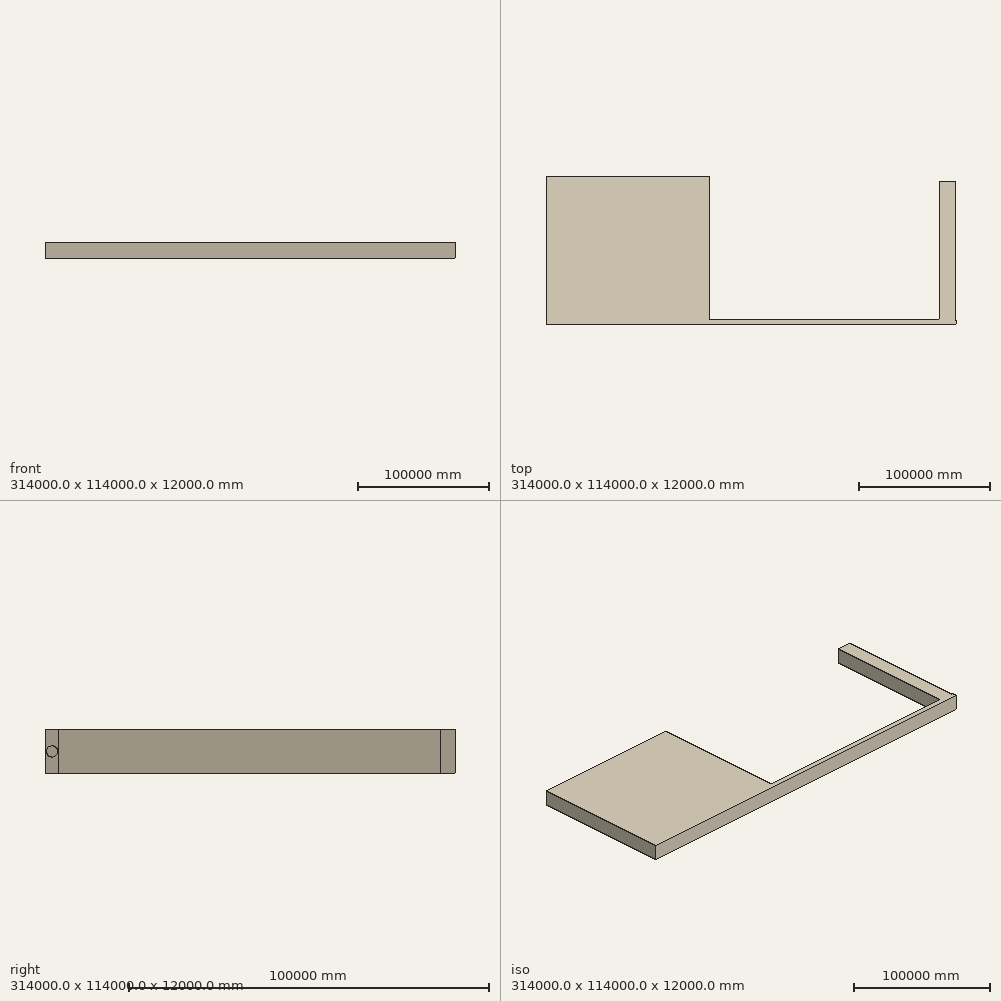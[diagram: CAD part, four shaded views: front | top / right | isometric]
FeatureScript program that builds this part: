
annotation { "Feature Type Name" : "Feature", "Feature Type Description" : "" }
export const myFeature = defineFeature(function(context is Context, id is Id, definition is map)
    precondition{}
    {
        {
            var Q0;
            Q0=qCreatedBy(makeId("Right.planeOp"),FACE);
            var sketch = newSketch(context, id + "F0", { "sketchPlane" : qUnion([Q0])});
            skLineSegment(sketch, "E0.bottom", {"start": v(1700, 5700) * mm, "end": v(-1700, 5700) * mm});
            skLineSegment(sketch, "E0.top", {"start": v(1700, -5700) * mm, "end": v(-1700, -5700) * mm});
            skLineSegment(sketch, "E0.left", {"start": v(1700, 5700) * mm, "end": v(1700, -5700) * mm});
            skLineSegment(sketch, "E0.right", {"start": v(-1700, 5700) * mm, "end": v(-1700, -5700) * mm});
            skPoint(sketch, "E0.middle", {"position": v(0, 0) * mm});
            skSolve(sketch);
        }
        {
            var Q0;
            Q0=makeQuery(id+"F0.imprint","IMPRINT",FACE,{"disambiguationData":[TD([[makeQuery(id+"F0.imprint","IMPRINT",EDGE,{"derivedFrom":sQuery(id+"F0.wireOp",EDGE,"E0.bottom")}),1.0]])]});
            var sketch = newSketch(context, id + "F1", { "sketchPlane" : qUnion([Q0])});
            skLineSegment(sketch, "E1.bottom", {"start": v(2000, 6000) * mm, "end": v(-2000, 6000) * mm});
            skLineSegment(sketch, "E1.top", {"start": v(2000, -6000) * mm, "end": v(-2000, -6000) * mm});
            skLineSegment(sketch, "E1.left", {"start": v(2000, 6000) * mm, "end": v(2000, -6000) * mm});
            skLineSegment(sketch, "E1.right", {"start": v(-2000, 6000) * mm, "end": v(-2000, -6000) * mm});
            skPoint(sketch, "E1.middle", {"position": v(0, 0) * mm});
            skSolve(sketch);
        }
        {
            var Q0;
            Q0=makeQuery(id+"F1.imprint","IMPRINT",FACE,{"disambiguationData":[TD([[makeQuery(id+"F1.imprint","IMPRINT",EDGE,{"derivedFrom":sQuery(id+"F1.wireOp",EDGE,"E1.bottom")}),1.0]])]});
            extrude(context, id + "F2", {"entities" : qUnion([Q0]), "oppositeDirection" : true, "depth" : 200000 * mm, "offsetDistance" : 25 * mm});
        }
        {
            var Q0;
            Q0=makeQuery(id+"F2.opExtrude","SWEPT_FACE",FACE,{"disambiguationData":[OSD([sQuery(id+"F1.wireOp",EDGE,"E1.left")])]});
            var sketch = newSketch(context, id + "F3", { "sketchPlane" : qUnion([Q0])});
            skCircle(sketch, "E2", {"center": v(-6000, 0) * mm, "radius": 6000 * mm});
            skCircle(sketch, "E3", {"center": v(-6000, 0) * mm, "radius": 5475 * mm});
            skLineSegment(sketch, "E4", {"start": v(0, 6000) * mm, "end": v(-6000, 6000) * mm});
            skLineSegment(sketch, "E5", {"start": v(0, -6000) * mm, "end": v(-6000, -6000) * mm});
            skLineSegment(sketch, "E6", {"start": v(-6000, 6000) * mm, "end": v(-12000, 6000) * mm});
            skLineSegment(sketch, "E7", {"start": v(-12000, 6000) * mm, "end": v(-12000, 0) * mm});
            skLineSegment(sketch, "E8", {"start": v(-12000, 0) * mm, "end": v(-12000, -6000) * mm});
            skLineSegment(sketch, "E9", {"start": v(-12000, -6000) * mm, "end": v(-6000, -6000) * mm});
            skSolve(sketch);
        }
        {
            var Q0;
            {var subQ0=sQuery(id+"F3.wireOp",EDGE,"E4");Q0=makeQuery(id+"F3.imprint","IMPRINT",FACE,{"disambiguationData":[TD([[makeQuery(id+"F3.imprint","IMPRINT",EDGE,{"derivedFrom":subQ0}),1.0]])]});}
            var Q1;
            {var subQ0=sQuery(id+"F3.wireOp",EDGE,"E6");Q1=makeQuery(id+"F3.imprint","IMPRINT",FACE,{"disambiguationData":[TD([[makeQuery(id+"F3.imprint","IMPRINT",EDGE,{"derivedFrom":subQ0}),1.0]])]});}
            var Q2;
            {var subQ2=sQuery(id+"F3.wireOp",EDGE,"E8");Q2=makeQuery(id+"F3.imprint","IMPRINT",FACE,{"disambiguationData":[TD([[makeQuery(id+"F3.imprint","IMPRINT",EDGE,{"derivedFrom":subQ2}),1.0]])]});}
            var Q3;
            {var subQ0=sQuery(id+"F3.wireOp",EDGE,"E5");Q3=makeQuery(id+"F3.imprint","IMPRINT",FACE,{"disambiguationData":[TD([[makeQuery(id+"F3.imprint","IMPRINT",EDGE,{"derivedFrom":subQ0}),-1.0]])]});}
            var Q4;
            Q4=makeQuery(id+"F3.imprint","IMPRINT",FACE,{"disambiguationData":[TD([[makeQuery(id+"F3.imprint","IMPRINT",EDGE,{"derivedFrom":sQuery(id+"F3.wireOp",EDGE,"E3")}),-1.0]])]});
            extrude(context, id + "F4", {"entities" : qUnion([Q0, Q1, Q2, Q3, Q4]), "operationType" : NewBodyOperationType.ADD, "oppositeDirection" : true, "depth" : 600 * mm, "offsetDistance" : 25 * mm});
        }
        {
            var Q0;
            Q0=makeQuery(id+"F4.opExtrude","CAP_FACE",FACE,{"disambiguationData":[OSD([sQuery(id+"F1.wireOp",EDGE,"E1.left"),sQuery(id+"F3.wireOp",EDGE,"E3"),sQuery(id+"F3.wireOp",EDGE,"E4"),sQuery(id+"F3.wireOp",EDGE,"E5"),sQuery(id+"F3.wireOp",EDGE,"E6"),sQuery(id+"F3.wireOp",EDGE,"E7"),sQuery(id+"F3.wireOp",EDGE,"E8"),sQuery(id+"F3.wireOp",EDGE,"E9")])],"isStart":false});
            extrude(context, id + "F5", {"entities" : qUnion([Q0]), "operationType" : NewBodyOperationType.ADD, "oppositeDirection" : true, "depth" : 105500 * mm, "offsetDistance" : 25 * mm});
        }
        {
            var Q0;
            Q0=makeQuery(id+"F2.opExtrude","CAP_FACE",FACE,{"disambiguationData":[OSD([sQuery(id+"F0.wireOp",EDGE,"E0.bottom"),sQuery(id+"F0.wireOp",EDGE,"E0.top"),sQuery(id+"F0.wireOp",EDGE,"E0.left"),sQuery(id+"F0.wireOp",EDGE,"E0.right"),sQuery(id+"F1.wireOp",EDGE,"E1.bottom"),sQuery(id+"F1.wireOp",EDGE,"E1.top"),sQuery(id+"F1.wireOp",EDGE,"E1.left"),sQuery(id+"F1.wireOp",EDGE,"E1.right")])],"isStart":true});
            extrude(context, id + "F6", {"entities" : qUnion([Q0]), "operationType" : NewBodyOperationType.ADD, "depth" : 12000 * mm, "offsetDistance" : 25 * mm});
        }
        {
            var Q0;
            {var subQ0=sQuery(id+"F3.wireOp",EDGE,"E8");var subQ1=sQuery(id+"F3.wireOp",EDGE,"E7");Q0=makeQuery(id+"F6.boolean.opBoolean","MERGE",FACE,{"derivedFrom":[makeQuery(id+"F5.boolean.opBoolean","MERGE",FACE,{"derivedFrom":[makeQuery(id+"F4.opExtrude","SWEPT_FACE",FACE,{"disambiguationData":[OSD([subQ1,subQ0])]}),makeQuery(id+"F5.opExtrude","SWEPT_FACE",FACE,{"disambiguationData":[OSD([subQ1,subQ0])]})]}),makeQuery(id+"F6.opExtrude","CAP_FACE",FACE,{"disambiguationData":[OSD([sQuery(id+"F0.wireOp",EDGE,"E0.bottom"),sQuery(id+"F0.wireOp",EDGE,"E0.top"),sQuery(id+"F0.wireOp",EDGE,"E0.left"),sQuery(id+"F0.wireOp",EDGE,"E0.right"),sQuery(id+"F1.wireOp",EDGE,"E1.bottom"),sQuery(id+"F1.wireOp",EDGE,"E1.top"),sQuery(id+"F1.wireOp",EDGE,"E1.left"),sQuery(id+"F1.wireOp",EDGE,"E1.right")])],"isStart":false})]});}
            var sketch = newSketch(context, id + "F7", { "sketchPlane" : qUnion([Q0])});
            skCircle(sketch, "E10", {"center": v(-150, 0) * mm, "radius": 1850 * mm});
            skCircle(sketch, "E11", {"center": v(-150, 0) * mm, "radius": 1550 * mm});
            skLineSegment(sketch, "E12", {"start": v(1700, 0) * mm, "end": v(1700, 6000) * mm});
            skLineSegment(sketch, "E13", {"start": v(1700, 6000) * mm, "end": v(-2000, 6000) * mm});
            skLineSegment(sketch, "E14", {"start": v(-2000, 6000) * mm, "end": v(-2000, 0) * mm});
            skLineSegment(sketch, "E15", {"start": v(-2000, 0) * mm, "end": v(-2000, -6000) * mm});
            skLineSegment(sketch, "E16", {"start": v(-2000, -6000) * mm, "end": v(1700, -6000) * mm});
            skLineSegment(sketch, "E17", {"start": v(1700, -6000) * mm, "end": v(1700, 0) * mm});
            skSolve(sketch);
        }
        {
            var Q0;
            {var subQ0=sQuery(id+"F7.wireOp",EDGE,"E12");Q0=makeQuery(id+"F7.imprint","IMPRINT",FACE,{"disambiguationData":[TD([[makeQuery(id+"F7.imprint","IMPRINT",EDGE,{"derivedFrom":subQ0}),1.0]])]});}
            var Q1;
            {var subQ5=makeQuery(id+"F6.opExtrude","CAP_EDGE",EDGE,{"disambiguationData":[OSD([sQuery(id+"F0.wireOp",EDGE,"E0.bottom")])],"isStart":false});Q1=makeQuery(id+"F7.imprint","IMPRINT",FACE,{"disambiguationData":[TD([[makeQuery(id+"F7.imprint","IMPRINT",EDGE,{"derivedFrom":subQ5}),1.0]])]});}
            var Q2;
            {var subQ5=makeQuery(id+"F6.opExtrude","CAP_EDGE",EDGE,{"disambiguationData":[OSD([sQuery(id+"F0.wireOp",EDGE,"E0.top")])],"isStart":false});Q2=makeQuery(id+"F7.imprint","IMPRINT",FACE,{"disambiguationData":[TD([[makeQuery(id+"F7.imprint","IMPRINT",EDGE,{"derivedFrom":subQ5}),-1.0]])]});}
            var Q3;
            {var subQ0=sQuery(id+"F7.wireOp",EDGE,"E15");Q3=makeQuery(id+"F7.imprint","IMPRINT",FACE,{"disambiguationData":[TD([[makeQuery(id+"F7.imprint","IMPRINT",EDGE,{"derivedFrom":subQ0}),1.0]])]});}
            var Q4;
            {var subQ0=sQuery(id+"F7.wireOp",EDGE,"E10");var subQ1=makeQuery(id+"F7.imprint","INTERSECT",VERTEX,{"derivedFrom":[subQ0,sQuery(id+"F7.wireOp",EDGE,"E12"),sQuery(id+"F7.wireOp",EDGE,"E17")]});Q4=makeQuery(id+"F7.imprint","IMPRINT",FACE,{"disambiguationData":[TD([[makeQuery(id+"F7.imprint","IMPRINT",EDGE,{"disambiguationData":[TD([[subQ1,-1.0]])],"derivedFrom":subQ0}),1.0]])]});}
            var Q5;
            {var subQ0=sQuery(id+"F7.wireOp",EDGE,"E10");var subQ2=makeQuery(id+"F6.opExtrude","CAP_EDGE",EDGE,{"disambiguationData":[OSD([sQuery(id+"F0.wireOp",EDGE,"E0.right")])],"isStart":false});var subQ3=makeQuery(id+"F7.imprint","INTERSECT",VERTEX,{"disambiguationData":[OD(0.0)],"derivedFrom":[subQ2,subQ0]});Q5=makeQuery(id+"F7.imprint","IMPRINT",FACE,{"disambiguationData":[TD([[makeQuery(id+"F7.imprint","IMPRINT",EDGE,{"disambiguationData":[TD([[subQ3,-1.0]])],"derivedFrom":subQ2}),-1.0]])]});}
            var Q6;
            {var subQ0=sQuery(id+"F7.wireOp",EDGE,"E10");var subQ3=makeQuery(id+"F6.opExtrude","CAP_EDGE",EDGE,{"disambiguationData":[OSD([sQuery(id+"F0.wireOp",EDGE,"E0.right")])],"isStart":false});var subQ4=makeQuery(id+"F7.imprint","INTERSECT",VERTEX,{"disambiguationData":[OD(0.0)],"derivedFrom":[subQ3,subQ0]});Q6=makeQuery(id+"F7.imprint","IMPRINT",FACE,{"disambiguationData":[TD([[makeQuery(id+"F7.imprint","IMPRINT",EDGE,{"disambiguationData":[TD([[subQ4,-1.0]])],"derivedFrom":subQ3}),1.0]])]});}
            var Q7;
            {var subQ0=sQuery(id+"F7.wireOp",EDGE,"E10");var subQ1=makeQuery(id+"F6.opExtrude","CAP_EDGE",EDGE,{"disambiguationData":[OSD([sQuery(id+"F0.wireOp",EDGE,"E0.right")])],"isStart":false});var subQ2=makeQuery(id+"F7.imprint","INTERSECT",VERTEX,{"disambiguationData":[OD(1.0)],"derivedFrom":[subQ1,subQ0]});Q7=makeQuery(id+"F7.imprint","IMPRINT",FACE,{"disambiguationData":[TD([[makeQuery(id+"F7.imprint","IMPRINT",EDGE,{"disambiguationData":[TD([[subQ2,1.0]])],"derivedFrom":subQ1}),1.0]])]});}
            extrude(context, id + "F8", {"entities" : qUnion([Q0, Q1, Q2, Q3, Q4, Q5, Q6, Q7]), "operationType" : NewBodyOperationType.ADD, "depth" : 1000 * mm, "offsetDistance" : 25 * mm});
        }
        {
            var Q0;
            Q0=makeQuery(id+"F8.opExtrude","CAP_FACE",FACE,{"disambiguationData":[OSD([sQuery(id+"F7.wireOp",EDGE,"E11"),sQuery(id+"F7.wireOp",EDGE,"E12"),sQuery(id+"F7.wireOp",EDGE,"E13"),sQuery(id+"F7.wireOp",EDGE,"E14"),sQuery(id+"F7.wireOp",EDGE,"E15"),sQuery(id+"F7.wireOp",EDGE,"E16"),sQuery(id+"F7.wireOp",EDGE,"E17")])],"isStart":false});
            cPlane(context, id + "F9", {"entities" : qUnion([Q0]), "cplaneType" : CPlaneType.OFFSET, "offset" : 150000 * mm, "width" : 150 * mm, "height" : 150 * mm});
        }
        {
            var Q0;
            Q0=qCreatedBy(id+"F9.planeOp",FACE);
            var sketch = newSketch(context, id + "F10", { "sketchPlane" : qUnion([Q0])});
            skPoint(sketch, "E18", {"position": v(-150, 0) * mm});
            skPoint(sketch, "E19", {"position": v(-150150, 0) * mm});
            skCircle(sketch, "E20", {"center": v(-150150, 0) * mm, "radius": 1850 * mm});
            skCircle(sketch, "E21", {"center": v(-150150, 0) * mm, "radius": 1550 * mm});
            skSolve(sketch);
        }
        {
            var Q0;
            Q0=makeQuery(id+"F8.opExtrude","CAP_EDGE",EDGE,{"disambiguationData":[OSD([sQuery(id+"F7.wireOp",EDGE,"E11")])],"isStart":false});
            var Q1;
            Q1=sQuery(id+"F10.wireOp",EDGE,"E21");
            loft(context, id + "F11", {"bodyType" : ToolBodyType.SURFACE, "wireProfilesArray" : [{ "wireProfileEntities" : qUnion([Q0]) }, { "wireProfileEntities" : qUnion([Q1]) }]});
        }
        {
            var Q0;
            Q0=makeQuery(id+"F5.opExtrude","CAP_FACE",FACE,{"disambiguationData":[OSD([sQuery(id+"F1.wireOp",EDGE,"E1.left"),sQuery(id+"F3.wireOp",EDGE,"E3"),sQuery(id+"F3.wireOp",EDGE,"E4"),sQuery(id+"F3.wireOp",EDGE,"E5"),sQuery(id+"F3.wireOp",EDGE,"E6"),sQuery(id+"F3.wireOp",EDGE,"E7"),sQuery(id+"F3.wireOp",EDGE,"E8"),sQuery(id+"F3.wireOp",EDGE,"E9")])],"isStart":false});
            var sketch = newSketch(context, id + "F12", { "sketchPlane" : qUnion([Q0])});
            skSolve(sketch);
        }
        {
            var Q0;
            Q0 = qSketchRegion(id + "F12", true);
            var Q1;
            Q1=makeQuery(id+"F12.imprint","IMPRINT",FACE,{"disambiguationData":[TD([[makeQuery(id+"F12.imprint","IMPRINT",EDGE,{"derivedFrom":makeQuery(id+"F5.opExtrude","CAP_EDGE",EDGE,{"disambiguationData":[OSD([sQuery(id+"F3.wireOp",EDGE,"E3")])],"isStart":false})}),1.0]])]});
            var Q2;
            Q2=makeQuery(id+"F12.imprint","IMPRINT",FACE,{"disambiguationData":[TD([[makeQuery(id+"F12.imprint","IMPRINT",EDGE,{"derivedFrom":makeQuery(id+"F5.opExtrude","CAP_EDGE",EDGE,{"disambiguationData":[OSD([sQuery(id+"F3.wireOp",EDGE,"E3")])],"isStart":false})}),-1.0]])]});
            extrude(context, id + "F13", {"entities" : qUnion([Q0, Q1, Q2]), "operationType" : NewBodyOperationType.ADD, "depth" : 1000 * mm, "offsetDistance" : 25 * mm});
        }
        {
            var Q0;
            Q0=makeQuery(id+"F2.opExtrude","CAP_FACE",FACE,{"disambiguationData":[OSD([sQuery(id+"F0.wireOp",EDGE,"E0.bottom"),sQuery(id+"F0.wireOp",EDGE,"E0.top"),sQuery(id+"F0.wireOp",EDGE,"E0.left"),sQuery(id+"F0.wireOp",EDGE,"E0.right"),sQuery(id+"F1.wireOp",EDGE,"E1.bottom"),sQuery(id+"F1.wireOp",EDGE,"E1.top"),sQuery(id+"F1.wireOp",EDGE,"E1.left"),sQuery(id+"F1.wireOp",EDGE,"E1.right")])],"isStart":false});
            var sketch = newSketch(context, id + "F14", { "sketchPlane" : qUnion([Q0])});
            skLineSegment(sketch, "E22", {"start": v(-1700, 5700) * mm, "end": v(-1700, 6000) * mm});
            skLineSegment(sketch, "E23", {"start": v(-1700, -5700) * mm, "end": v(-1700, -6000) * mm});
            skLineSegment(sketch, "E24", {"start": v(-1700, 5700) * mm, "end": v(1700, 5700) * mm});
            skLineSegment(sketch, "E25", {"start": v(1700, 5700) * mm, "end": v(1700, -5700) * mm});
            skLineSegment(sketch, "E26", {"start": v(1700, -5700) * mm, "end": v(-1700, -5700) * mm});
            skLineSegment(sketch, "E27", {"start": v(-1700, -6000) * mm, "end": v(2000, -6000) * mm});
            skLineSegment(sketch, "E28", {"start": v(2000, -6000) * mm, "end": v(2000, 6000) * mm});
            skLineSegment(sketch, "E29", {"start": v(2000, 6000) * mm, "end": v(-1700, 6000) * mm});
            skSolve(sketch);
        }
        {
            var Q0;
            Q0=makeQuery(id+"F14.imprint","IMPRINT",FACE,{"disambiguationData":[TD([[makeQuery(id+"F14.imprint","IMPRINT",EDGE,{"derivedFrom":sQuery(id+"F14.wireOp",EDGE,"E22")}),-1.0]])]});
            extrude(context, id + "F15", {"entities" : qUnion([Q0]), "operationType" : NewBodyOperationType.ADD, "depth" : 100000 * mm, "offsetDistance" : 25 * mm});
        }
        {
            var Q0;
            Q0=makeQuery(id+"F15.opExtrude","CAP_FACE",FACE,{"disambiguationData":[OSD([sQuery(id+"F14.wireOp",EDGE,"E22"),sQuery(id+"F14.wireOp",EDGE,"E23"),sQuery(id+"F14.wireOp",EDGE,"E24"),sQuery(id+"F14.wireOp",EDGE,"E25"),sQuery(id+"F14.wireOp",EDGE,"E26"),sQuery(id+"F14.wireOp",EDGE,"E27"),sQuery(id+"F14.wireOp",EDGE,"E28"),sQuery(id+"F14.wireOp",EDGE,"E29")])],"isStart":false});
            var sketch = newSketch(context, id + "F16", { "sketchPlane" : qUnion([Q0])});
            skLineSegment(sketch, "E30", {"start": v(-1700, -6000) * mm, "end": v(-1700, 6000) * mm});
            skLineSegment(sketch, "E31", {"start": v(-1700, 6000) * mm, "end": v(2000, 6000) * mm});
            skLineSegment(sketch, "E32", {"start": v(2000, 6000) * mm, "end": v(2000, -6000) * mm});
            skLineSegment(sketch, "E33", {"start": v(2000, -6000) * mm, "end": v(-1700, -6000) * mm});
            skSolve(sketch);
        }
        {
            var Q0;
            {var subQ0=sQuery(id+"F16.wireOp",EDGE,"E31");Q0=makeQuery(id+"F16.imprint","IMPRINT",FACE,{"disambiguationData":[TD([[makeQuery(id+"F16.imprint","IMPRINT",EDGE,{"derivedFrom":subQ0}),-1.0]])]});}
            var Q1;
            {var subQ1=makeQuery(id+"F15.opExtrude","CAP_EDGE",EDGE,{"disambiguationData":[OSD([sQuery(id+"F14.wireOp",EDGE,"E24")])],"isStart":false});Q1=makeQuery(id+"F16.imprint","IMPRINT",FACE,{"disambiguationData":[TD([[makeQuery(id+"F16.imprint","IMPRINT",EDGE,{"derivedFrom":subQ1}),-1.0]])]});}
            extrude(context, id + "F17", {"entities" : qUnion([Q0, Q1]), "operationType" : NewBodyOperationType.ADD, "depth" : 1000 * mm, "offsetDistance" : 25 * mm});
        }
        {
            var Q0;
            Q0=makeQuery(id+"F17.boolean.opBoolean","MERGE",FACE,{"derivedFrom":[makeQuery(id+"F15.opExtrude","SWEPT_FACE",FACE,{"disambiguationData":[OSD([sQuery(id+"F14.wireOp",EDGE,"E22")])]}),makeQuery(id+"F15.opExtrude","SWEPT_FACE",FACE,{"disambiguationData":[OSD([sQuery(id+"F14.wireOp",EDGE,"E23")])]}),makeQuery(id+"F17.opExtrude","SWEPT_FACE",FACE,{"disambiguationData":[OSD([sQuery(id+"F16.wireOp",EDGE,"E30")])]})]});
            extrude(context, id + "F18", {"entities" : qUnion([Q0]), "operationType" : NewBodyOperationType.ADD, "depth" : 300 * mm, "offsetDistance" : 25 * mm});
        }
        {
            var Q0;
            {var subQ0=sQuery(id+"F1.wireOp",EDGE,"E1.left");Q0=makeQuery(id+"F18.boolean.opBoolean","MERGE",FACE,{"derivedFrom":[makeQuery(id+"F4.boolean.opBoolean","MERGE",FACE,{"derivedFrom":[makeQuery(id+"F2.opExtrude","SWEPT_FACE",FACE,{"disambiguationData":[OSD([subQ0])]}),makeQuery(id+"F4.opExtrude","CAP_FACE",FACE,{"disambiguationData":[OSD([subQ0,sQuery(id+"F3.wireOp",EDGE,"E3"),sQuery(id+"F3.wireOp",EDGE,"E4"),sQuery(id+"F3.wireOp",EDGE,"E5"),sQuery(id+"F3.wireOp",EDGE,"E6"),sQuery(id+"F3.wireOp",EDGE,"E7"),sQuery(id+"F3.wireOp",EDGE,"E8"),sQuery(id+"F3.wireOp",EDGE,"E9")])],"isStart":true})]}),makeQuery(id+"F18.opExtrude","CAP_FACE",FACE,{"disambiguationData":[OSD([sQuery(id+"F14.wireOp",EDGE,"E22"),sQuery(id+"F14.wireOp",EDGE,"E23"),sQuery(id+"F16.wireOp",EDGE,"E30")])],"isStart":false})]});}
            var sketch = newSketch(context, id + "F19", { "sketchPlane" : qUnion([Q0])});
            skLineSegment(sketch, "E34", {"start": v(301000, -6000) * mm, "end": v(176000, -6000) * mm});
            skLineSegment(sketch, "E35", {"start": v(301000, -6000) * mm, "end": v(301000, 6000) * mm});
            skLineSegment(sketch, "E36", {"start": v(301000, 6000) * mm, "end": v(176000, 6000) * mm});
            skLineSegment(sketch, "E37", {"start": v(176000, 6000) * mm, "end": v(176000, -6000) * mm});
            skSolve(sketch);
        }
        {
            var Q0;
            Q0=makeQuery(id+"F19.imprint","IMPRINT",FACE,{"disambiguationData":[TD([[makeQuery(id+"F19.imprint","IMPRINT",EDGE,{"derivedFrom":sQuery(id+"F19.wireOp",EDGE,"E34")}),-1.0]])]});
            extrude(context, id + "F20", {"entities" : qUnion([Q0]), "operationType" : NewBodyOperationType.ADD, "depth" : 110000 * mm, "offsetDistance" : 25 * mm});
        }
    });
